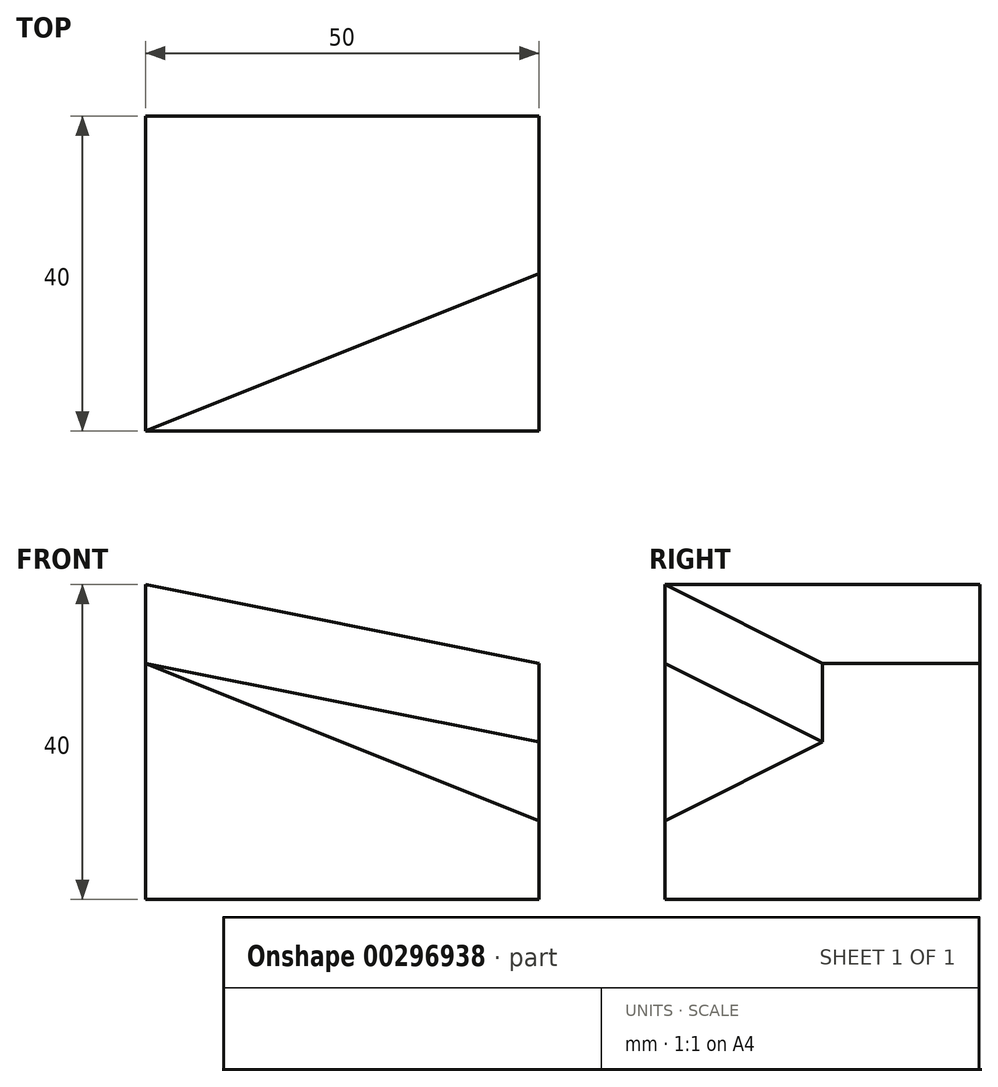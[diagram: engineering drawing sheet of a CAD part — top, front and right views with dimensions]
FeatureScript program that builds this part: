
annotation { "Feature Type Name" : "Feature", "Feature Type Description" : "" }
export const myFeature = defineFeature(function(context is Context, id is Id, definition is map)
    precondition{}
    {
        {
            var Q0;
            Q0=qCreatedBy(makeId("Front.planeOp"),FACE);
            var sketch = newSketch(context, id + "F0", { "sketchPlane" : qUnion([Q0])});
            skLineSegment(sketch, "E0.bottom", {"start": v(0, 0) * mm, "end": v(50, 0) * mm});
            skLineSegment(sketch, "E0.top", {"start": v(0, 40) * mm, "end": v(50, 40) * mm});
            skLineSegment(sketch, "E0.left", {"start": v(0, 0) * mm, "end": v(0, 40) * mm});
            skLineSegment(sketch, "E0.right", {"start": v(50, 0) * mm, "end": v(50, 40) * mm});
            skLineSegment(sketch, "E1", {"start": v(0, 30) * mm, "end": v(50, 20) * mm});
            skSolve(sketch);
        }
        {
            var Q0;
            {var subQ0=sQuery(id+"F0.wireOp",EDGE,"jSzgsLXq-SLkg-gTy4-seES-EWGS3kPx2e71.bottom");Q0=makeQuery(id+"F0.imprint","IMPRINT",FACE,{"disambiguationData":[TD([[makeQuery(id+"F0.imprint","IMPRINT",EDGE,{"derivedFrom":subQ0}),1.0]])]});}
            var Q1;
            {var subQ0=sQuery(id+"F0.wireOp",EDGE,"E0.bottom");Q1=makeQuery(id+"F0.imprint","IMPRINT",FACE,{"disambiguationData":[TD([[makeQuery(id+"F0.imprint","IMPRINT",EDGE,{"derivedFrom":subQ0}),1.0]])]});}
            extrude(context, id + "F1", {"entities" : qUnion([Q0, Q1]), "depth" : 40 * mm, "symmetric" : true});
        }
        {
            var Q0;
            Q0=makeQuery(id+"F1.opExtrude","SWEPT_EDGE",EDGE,{"disambiguationData":[OSD([sQuery(id+"F0.wireOp",EDGE,"E0.right"),sQuery(id+"F0.wireOp",EDGE,"E1")])]});
            cPoint(context, id + "F2", {"entities" : qUnion([Q0]), "parameter" : 0.5});
        }
        {
            var Q0;
            Q0=makeQuery(id+"F1.opExtrude","CAP_EDGE",EDGE,{"disambiguationData":[OSD([sQuery(id+"F0.wireOp",EDGE,"E0.right")])],"isStart":false});
            cPoint(context, id + "F3", {"entities" : qUnion([Q0]), "parameter" : 0.5});
        }
        {
            var Q0;
            Q0 = qCreatedBy(id + "F2" ,VERTEX);
            var Q1;
            Q1=makeQuery(id+"F1.opExtrude","CAP_VERTEX",VERTEX,{"disambiguationData":[OSD([sQuery(id+"F0.wireOp",EDGE,"E0.left"),sQuery(id+"F0.wireOp",EDGE,"E1")])],"isStart":false});
            var Q2;
            Q2 = qCreatedBy(id + "F3" ,VERTEX);
            cPlane(context, id + "F4", {"entities" : qUnion([Q0, Q1, Q2]), "cplaneType" : CPlaneType.THREE_POINT, "offset" : 25 * mm, "width" : 150 * mm, "height" : 150 * mm});
        }
        {
            var Q0;
            Q0=qCreatedBy(id+"F4.planeOp",FACE);
            var sketch = newSketch(context, id + "F5", { "sketchPlane" : qUnion([Q0])});
            skPoint(sketch, "E2.0", {"position": v(-12.05, 4.47) * mm});
            skPoint(sketch, "E3.0", {"position": v(41.05, -8.94) * mm});
            skPoint(sketch, "E4.0", {"position": v(41.05, 13.42) * mm});
            skLineSegment(sketch, "E5", {"start": v(-12.05, 4.47) * mm, "end": v(41.05, -8.94) * mm});
            skLineSegment(sketch, "E6", {"start": v(41.05, 13.42) * mm, "end": v(41.05, -8.94) * mm});
            skLineSegment(sketch, "E7", {"start": v(41.05, 13.42) * mm, "end": v(-12.05, 4.47) * mm});
            skSolve(sketch);
        }
        {
            var Q0;
            Q0 = qSketchRegion(id + "F5", true);
            extrude(context, id + "F6", {"entities" : qUnion([Q0]), "operationType" : NewBodyOperationType.REMOVE, "endBound" : BoundingType.THROUGH_ALL, "oppositeDirection" : true, "depth" : 25 * mm});
        }
        {
            var Q0;
            Q0=makeQuery(id+"F1.opExtrude","SWEPT_FACE",FACE,{"disambiguationData":[OSD([sQuery(id+"F0.wireOp",EDGE,"E0.left")])]});
            var sketch = newSketch(context, id + "F7", { "sketchPlane" : qUnion([Q0])});
            skLineSegment(sketch, "E8", {"start": v(20, 30) * mm, "end": v(20, 40) * mm});
            skSolve(sketch);
        }
        {
            var Q0;
            Q0=makeQuery(id+"F1.opExtrude","SWEPT_FACE",FACE,{"disambiguationData":[OSD([sQuery(id+"F0.wireOp",EDGE,"E1")])]});
            var Q1;
            Q1=sQuery(id+"F7.wireOp",EDGE,"E8");
            sweep(context, id + "F8", {"operationType" : NewBodyOperationType.ADD, "profiles" : qUnion([Q0]), "path" : qUnion([Q1])});
        }
    });
